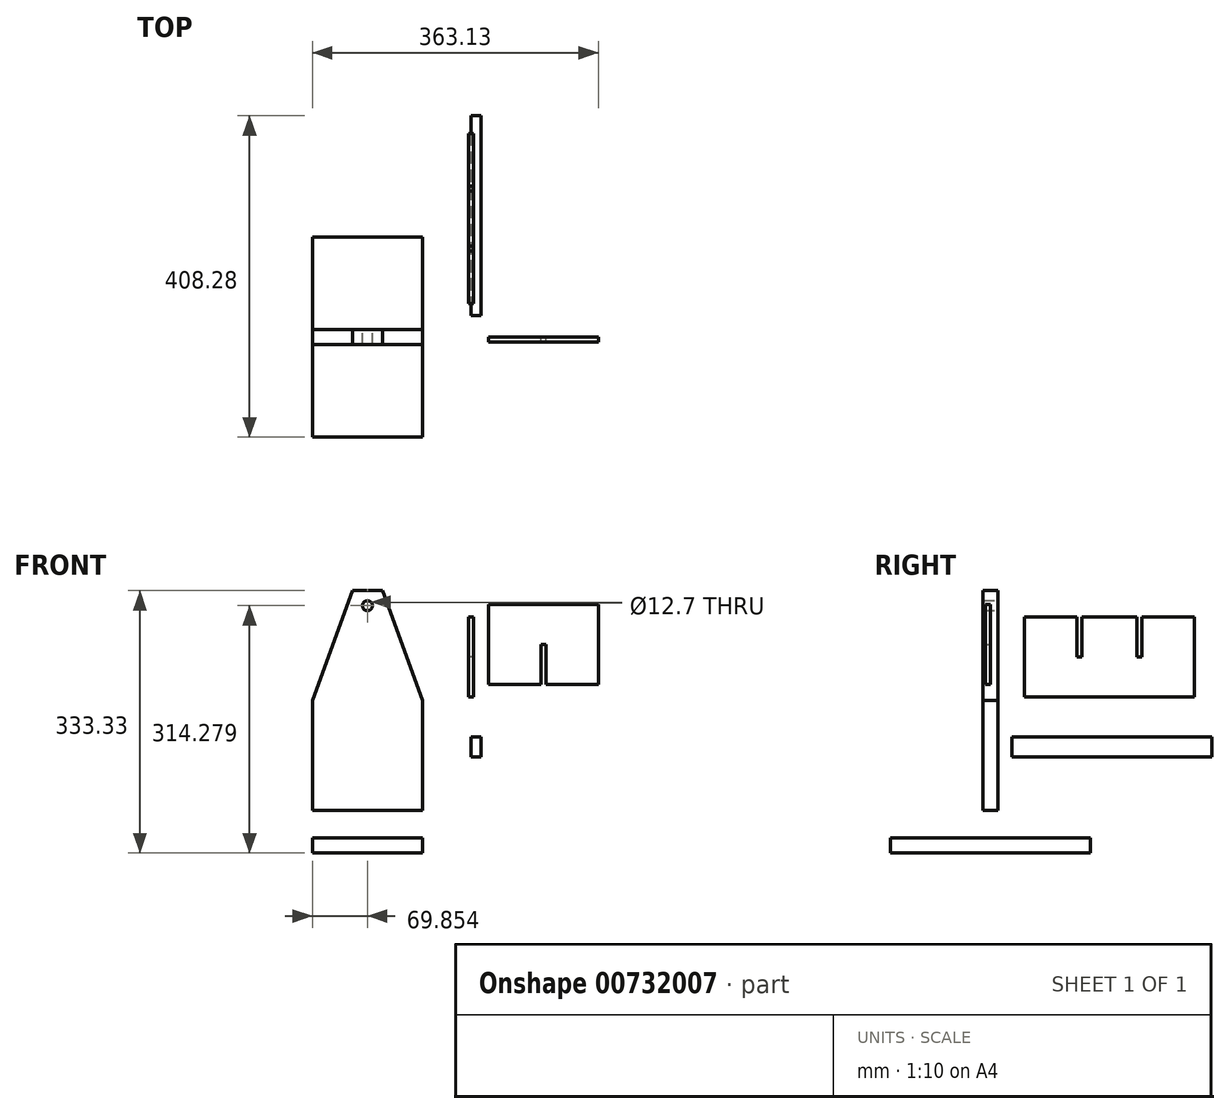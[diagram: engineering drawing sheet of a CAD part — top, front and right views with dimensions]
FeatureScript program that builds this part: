
annotation { "Feature Type Name" : "Feature", "Feature Type Description" : "" }
export const myFeature = defineFeature(function(context is Context, id is Id, definition is map)
    precondition{}
    {
        {
            var Q0;
            Q0=qCreatedBy(makeId("Front.planeOp"),FACE);
            var sketch = newSketch(context, id + "F0", { "sketchPlane" : qUnion([Q0])});
            skLineSegment(sketch, "E0.bottom", {"start": v(-61.47, -108.66) * mm, "end": v(-201.17, -108.66) * mm});
            skLineSegment(sketch, "E0.top", {"start": v(-61.47, -89.6) * mm, "end": v(-201.17, -89.6) * mm});
            skLineSegment(sketch, "E0.left", {"start": v(-61.47, -108.66) * mm, "end": v(-61.47, -89.6) * mm});
            skLineSegment(sketch, "E0.right", {"start": v(-201.17, -108.66) * mm, "end": v(-201.17, -89.6) * mm});
            skSolve(sketch);
        }
        {
            var Q0;
            Q0=qCreatedBy(makeId("Front.planeOp"),FACE);
            var sketch = newSketch(context, id + "F1", { "sketchPlane" : qUnion([Q0])});
            skLineSegment(sketch, "E1.bottom", {"start": v(-201.25, -54.73) * mm, "end": v(-61.55, -54.73) * mm});
            skLineSegment(sketch, "E1.left", {"start": v(-201.25, -54.73) * mm, "end": v(-201.25, 84.97) * mm});
            skLineSegment(sketch, "E1.right", {"start": v(-61.55, -54.73) * mm, "end": v(-61.55, 84.97) * mm});
            skCircle(sketch, "E2", {"center": v(-131.4, 205.62) * mm, "radius": 6.35 * mm});
            skLineSegment(sketch, "E3", {"start": v(-201.25, 84.97) * mm, "end": v(-150.45, 224.67) * mm});
            skLineSegment(sketch, "E4", {"start": v(-61.55, 84.97) * mm, "end": v(-112.35, 224.67) * mm});
            skLineSegment(sketch, "E5", {"start": v(-150.45, 224.67) * mm, "end": v(-112.35, 224.67) * mm});
            skSolve(sketch);
        }
        {
            var Q0;
            Q0=qCreatedBy(makeId("Right.planeOp"),FACE);
            var sketch = newSketch(context, id + "F2", { "sketchPlane" : qUnion([Q0])});
            skLineSegment(sketch, "E6.bottom", {"start": v(281.28, 13.21) * mm, "end": v(27.28, 13.21) * mm});
            skLineSegment(sketch, "E6.top", {"start": v(281.28, 38.61) * mm, "end": v(27.28, 38.61) * mm});
            skLineSegment(sketch, "E6.left", {"start": v(281.28, 13.21) * mm, "end": v(281.28, 38.61) * mm});
            skLineSegment(sketch, "E6.right", {"start": v(27.28, 13.21) * mm, "end": v(27.28, 38.61) * mm});
            skSolve(sketch);
        }
        {
            var Q0;
            Q0 = qSketchRegion(id + "F2", true);
            extrude(context, id + "F3", {"entities" : qUnion([Q0]), "depth" : 12.7 * mm, "offsetDistance" : 25.4 * mm});
        }
        {
            var Q0;
            Q0=makeQuery(id+"F1.imprint","IMPRINT",FACE,{"disambiguationData":[TD([[makeQuery(id+"F1.imprint","IMPRINT",EDGE,{"derivedFrom":sQuery(id+"F1.wireOp",EDGE,"E1.bottom")}),1.0]])]});
            extrude(context, id + "F4", {"entities" : qUnion([Q0]), "endBound" : BoundingType.SYMMETRIC, "depth" : 19.05 * mm, "offsetDistance" : 25.4 * mm});
        }
        {
            var Q0;
            Q0=makeQuery(id+"F0.imprint","IMPRINT",FACE,{"disambiguationData":[TD([[makeQuery(id+"F0.imprint","IMPRINT",EDGE,{"derivedFrom":sQuery(id+"F0.wireOp",EDGE,"E0.bottom")}),-1.0]])]});
            extrude(context, id + "F5", {"entities" : qUnion([Q0]), "endBound" : BoundingType.SYMMETRIC, "depth" : 254 * mm, "offsetDistance" : 25.4 * mm});
        }
        {
            var Q0;
            Q0=qCreatedBy(makeId("Right.planeOp"),FACE);
            var sketch = newSketch(context, id + "F6", { "sketchPlane" : qUnion([Q0])});
            skLineSegment(sketch, "E7", {"start": v(43, 89.81) * mm, "end": v(258.9, 89.81) * mm});
            skLineSegment(sketch, "E8", {"start": v(258.9, 89.81) * mm, "end": v(258.9, 191.41) * mm});
            skLineSegment(sketch, "E9", {"start": v(258.9, 191.41) * mm, "end": v(192.22, 191.41) * mm});
            skLineSegment(sketch, "E10", {"start": v(192.22, 191.41) * mm, "end": v(192.22, 140.61) * mm});
            skLineSegment(sketch, "E11", {"start": v(192.22, 140.61) * mm, "end": v(185.87, 140.61) * mm});
            skLineSegment(sketch, "E12", {"start": v(185.87, 140.61) * mm, "end": v(185.87, 191.41) * mm});
            skLineSegment(sketch, "E13", {"start": v(185.87, 191.41) * mm, "end": v(116.02, 191.41) * mm});
            skLineSegment(sketch, "E14", {"start": v(116.02, 191.41) * mm, "end": v(116.02, 140.61) * mm});
            skLineSegment(sketch, "E15", {"start": v(116.02, 140.61) * mm, "end": v(109.67, 140.61) * mm});
            skLineSegment(sketch, "E16", {"start": v(109.67, 140.61) * mm, "end": v(109.67, 191.41) * mm});
            skLineSegment(sketch, "E17", {"start": v(109.67, 191.41) * mm, "end": v(43, 191.41) * mm});
            skLineSegment(sketch, "E18", {"start": v(43, 191.41) * mm, "end": v(43, 89.81) * mm});
            skSolve(sketch);
        }
        {
            var Q0;
            Q0=makeQuery(id+"F6.imprint","IMPRINT",FACE,{"disambiguationData":[TD([[makeQuery(id+"F6.imprint","IMPRINT",EDGE,{"derivedFrom":sQuery(id+"F6.wireOp",EDGE,"E7")}),1.0]])]});
            extrude(context, id + "F7", {"entities" : qUnion([Q0]), "endBound" : BoundingType.SYMMETRIC, "depth" : 6.35 * mm, "offsetDistance" : 25.4 * mm});
        }
        {
            var Q0;
            Q0=qCreatedBy(makeId("Front.planeOp"),FACE);
            var sketch = newSketch(context, id + "F8", { "sketchPlane" : qUnion([Q0])});
            skLineSegment(sketch, "E19.top", {"start": v(161.88, 207.03) * mm, "end": v(22.18, 207.03) * mm});
            skLineSegment(sketch, "E19.left", {"start": v(161.88, 105.43) * mm, "end": v(161.88, 207.03) * mm});
            skLineSegment(sketch, "E19.right", {"start": v(22.18, 105.43) * mm, "end": v(22.18, 207.03) * mm});
            skLineSegment(sketch, "E20.top", {"start": v(95.2, 156.23) * mm, "end": v(88.85, 156.23) * mm});
            skLineSegment(sketch, "E20.left", {"start": v(95.2, 105.43) * mm, "end": v(95.2, 156.23) * mm});
            skLineSegment(sketch, "E20.right", {"start": v(88.85, 105.43) * mm, "end": v(88.85, 156.23) * mm});
            skLineSegment(sketch, "E21", {"start": v(161.88, 105.43) * mm, "end": v(95.2, 105.43) * mm});
            skLineSegment(sketch, "E22", {"start": v(88.85, 105.43) * mm, "end": v(22.18, 105.43) * mm});
            skSolve(sketch);
        }
        {
            var Q0;
            Q0=makeQuery(id+"F8.imprint","IMPRINT",FACE,{"disambiguationData":[TD([[makeQuery(id+"F8.imprint","IMPRINT",EDGE,{"derivedFrom":sQuery(id+"F8.wireOp",EDGE,"E19.top")}),1.0]])]});
            extrude(context, id + "F9", {"entities" : qUnion([Q0]), "depth" : 6.35 * mm, "offsetDistance" : 25.4 * mm});
        }
    });
